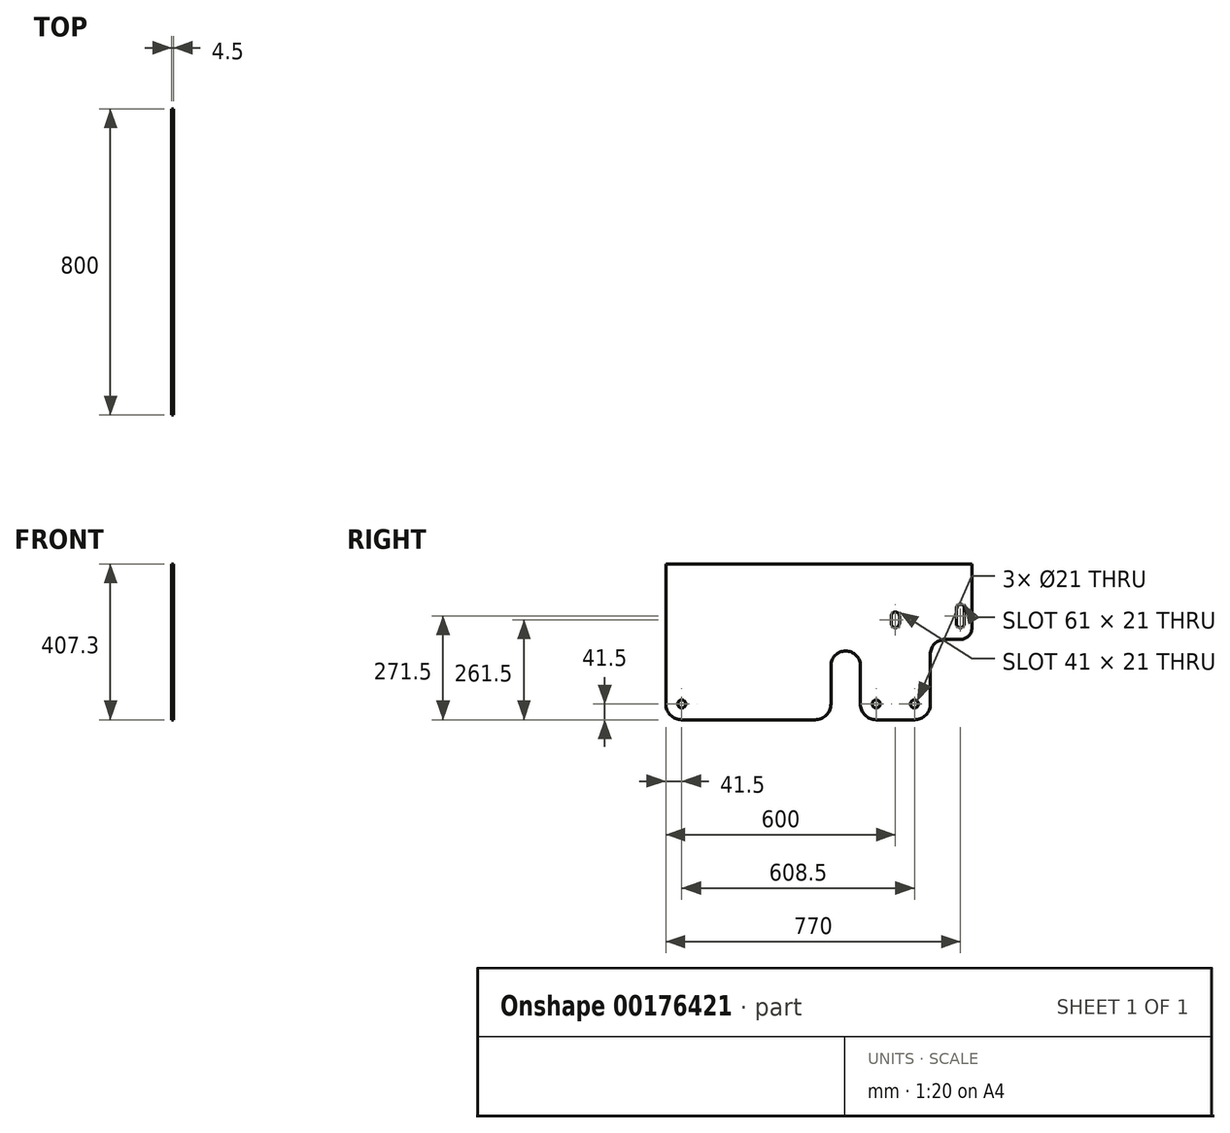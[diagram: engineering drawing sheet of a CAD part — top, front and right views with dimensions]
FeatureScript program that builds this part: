
annotation { "Feature Type Name" : "Feature", "Feature Type Description" : "" }
export const myFeature = defineFeature(function(context is Context, id is Id, definition is map)
    precondition{}
    {
        {
            var Q0;
            Q0=qCreatedBy(makeId("Right.planeOp"),FACE);
            var sketch = newSketch(context, id + "F0", { "sketchPlane" : qUnion([Q0])});
            skLineSegment(sketch, "E0", {"start": v(-34.06, -31.3) * mm, "end": v(-34.06, -31.3) * mm});
            skLineSegment(sketch, "E1", {"start": v(-800, -246.5) * mm, "end": v(-800, -79.2) * mm});
            skArc(sketch, "E2", {"start": v(-189.5, -215) * mm, "mid": v(-200, -204.5) * mm, "end": v(-210.5, -215) * mm});
            skArc(sketch, "E3", {"start": v(-70, -276.5) * mm, "mid": v(-97.22, -287.78) * mm, "end": v(-108.5, -315) * mm});
            skArc(sketch, "E4", {"start": v(-291.5, -345) * mm, "mid": v(-330, -306.5) * mm, "end": v(-368.5, -345) * mm});
            skLineSegment(sketch, "E5", {"start": v(-291.5, -445) * mm, "end": v(-291.5, -345) * mm});
            skLineSegment(sketch, "E6", {"start": v(-250, -486.5) * mm, "end": v(-150, -486.5) * mm});
            skLineSegment(sketch, "E7", {"start": v(-108.5, -445) * mm, "end": v(-108.5, -315) * mm});
            skLineSegment(sketch, "E8", {"start": v(-70, -276.5) * mm, "end": v(-30, -276.5) * mm});
            skCircle(sketch, "E9", {"center": v(-150, -445) * mm, "radius": 10.5 * mm});
            skPoint(sketch, "E10.visualSharp", {"position": v(0, -276.5) * mm});
            skCircle(sketch, "E11", {"center": v(-250, -445) * mm, "radius": 10.5 * mm});
            skPoint(sketch, "E12.visualSharp", {"position": v(-800, -486.5) * mm});
            skPoint(sketch, "E13.visualSharp", {"position": v(0, -486.5) * mm});
            skPoint(sketch, "E14.orphan", {"position": v(-800, 260.85) * mm});
            skLineSegment(sketch, "E15", {"start": v(-800, -79.2) * mm, "end": v(0, -79.2) * mm});
            skLineSegment(sketch, "E16", {"start": v(-368.5, -345) * mm, "end": v(-368.5, -445) * mm});
            skLineSegment(sketch, "E17", {"start": v(-410, -486.5) * mm, "end": v(-758.5, -486.5) * mm});
            skLineSegment(sketch, "E18", {"start": v(-800, -246.5) * mm, "end": v(-800, -445) * mm});
            skArc(sketch, "E19.filletArc", {"start": v(-800, -445) * mm, "mid": v(-787.84, -474.34) * mm, "end": v(-758.5, -486.5) * mm});
            skPoint(sketch, "E20.orphan", {"position": v(-108.5, -445) * mm});
            skPoint(sketch, "E21.orphan", {"position": v(-150, -486.5) * mm});
            skPoint(sketch, "E22.orphan", {"position": v(-250, -486.5) * mm});
            skPoint(sketch, "E23.orphan", {"position": v(-291.5, -445) * mm});
            skPoint(sketch, "E24.center.orphan", {"position": v(-410, -445) * mm});
            skPoint(sketch, "E25.orphan", {"position": v(-368.5, -445) * mm});
            skPoint(sketch, "E26.orphan", {"position": v(-410, -486.5) * mm});
            skPoint(sketch, "E27.visualSharp", {"position": v(-108.5, -486.5) * mm});
            skArc(sketch, "E27.filletArc", {"start": v(-150, -486.5) * mm, "mid": v(-120.66, -474.34) * mm, "end": v(-108.5, -445) * mm});
            skPoint(sketch, "E28.visualSharp", {"position": v(-291.5, -486.5) * mm});
            skArc(sketch, "E28.filletArc", {"start": v(-291.5, -445) * mm, "mid": v(-279.34, -474.34) * mm, "end": v(-250, -486.5) * mm});
            skPoint(sketch, "E29.visualSharp", {"position": v(-368.5, -486.5) * mm});
            skArc(sketch, "E29.filletArc", {"start": v(-410, -486.5) * mm, "mid": v(-380.66, -474.34) * mm, "end": v(-368.5, -445) * mm});
            skCircle(sketch, "E30", {"center": v(-758.5, -445) * mm, "radius": 10.5 * mm});
            skArc(sketch, "E31", {"start": v(-19.5, -195) * mm, "mid": v(-30, -184.5) * mm, "end": v(-40.5, -195) * mm});
            skArc(sketch, "E32", {"start": v(-40.5, -235) * mm, "mid": v(-30, -245.5) * mm, "end": v(-19.5, -235) * mm});
            skArc(sketch, "E33", {"start": v(-210.5, -235) * mm, "mid": v(-200, -245.5) * mm, "end": v(-189.5, -235) * mm});
            skLineSegment(sketch, "E34", {"start": v(-40.5, -195) * mm, "end": v(-40.5, -235) * mm});
            skLineSegment(sketch, "E35", {"start": v(-30, -195) * mm, "end": v(-19.5, -195) * mm});
            skLineSegment(sketch, "E36", {"start": v(-19.5, -195) * mm, "end": v(-19.5, -235) * mm});
            skLineSegment(sketch, "E37", {"start": v(-189.5, -235) * mm, "end": v(-189.5, -215) * mm});
            skLineSegment(sketch, "E38", {"start": v(-210.5, -235) * mm, "end": v(-210.5, -215) * mm});
            skPoint(sketch, "E39.visualSharp", {"position": v(0, -79.2) * mm});
            skArc(sketch, "E40.filletArc", {"start": v(-30, -276.5) * mm, "mid": v(-8.79, -267.71) * mm, "end": v(0, -246.5) * mm});
            skLineSegment(sketch, "E41", {"start": v(0, -246.5) * mm, "end": v(0, -79.2) * mm});
            skSolve(sketch);
        }
        {
            var Q0;
            {var subQ7=sQuery(id+"F0.wireOp",EDGE,"E1");Q0=makeQuery(id+"F0.imprint","IMPRINT",FACE,{"disambiguationData":[TD([[makeQuery(id+"F0.imprint","IMPRINT",EDGE,{"derivedFrom":subQ7}),-1.0]])]});}
            var Q1;
            {var subQ8=sQuery(id+"F0.wireOp",EDGE,"E16");Q1=makeQuery(id+"F0.imprint","IMPRINT",FACE,{"disambiguationData":[TD([[makeQuery(id+"F0.imprint","IMPRINT",EDGE,{"derivedFrom":subQ8}),-1.0]])]});}
            var Q2;
            {var subQ0=sQuery(id+"F0.wireOp",EDGE,"257c3554-e73b-4e7b-abe2-ba3002d2c040");var subQ1=makeQuery(id+"F0.imprint","INTERSECT",VERTEX,{"derivedFrom":[sQuery(id+"F0.wireOp",EDGE,"KGBynEQr-p8uO-Kr7x-SzVv-YDPi38DI9xJs"),subQ0]});Q2=makeQuery(id+"F0.imprint","IMPRINT",FACE,{"disambiguationData":[TD([[makeQuery(id+"F0.imprint","IMPRINT",EDGE,{"disambiguationData":[TD([[subQ1,1.0]])],"derivedFrom":subQ0}),1.0]])]});}
            var Q3;
            {var subQ2=sQuery(id+"F0.wireOp",EDGE,"91872a80-e428-49c4-8857-6d0e10d51c3a.filletArc");Q3=makeQuery(id+"F0.imprint","IMPRINT",FACE,{"disambiguationData":[TD([[makeQuery(id+"F0.imprint","IMPRINT",EDGE,{"derivedFrom":subQ2}),-1.0]])]});}
            extrude(context, id + "F1", {"entities" : qUnion([Q0, Q1, Q2, Q3]), "depth" : 4.5 * mm});
        }
    });
